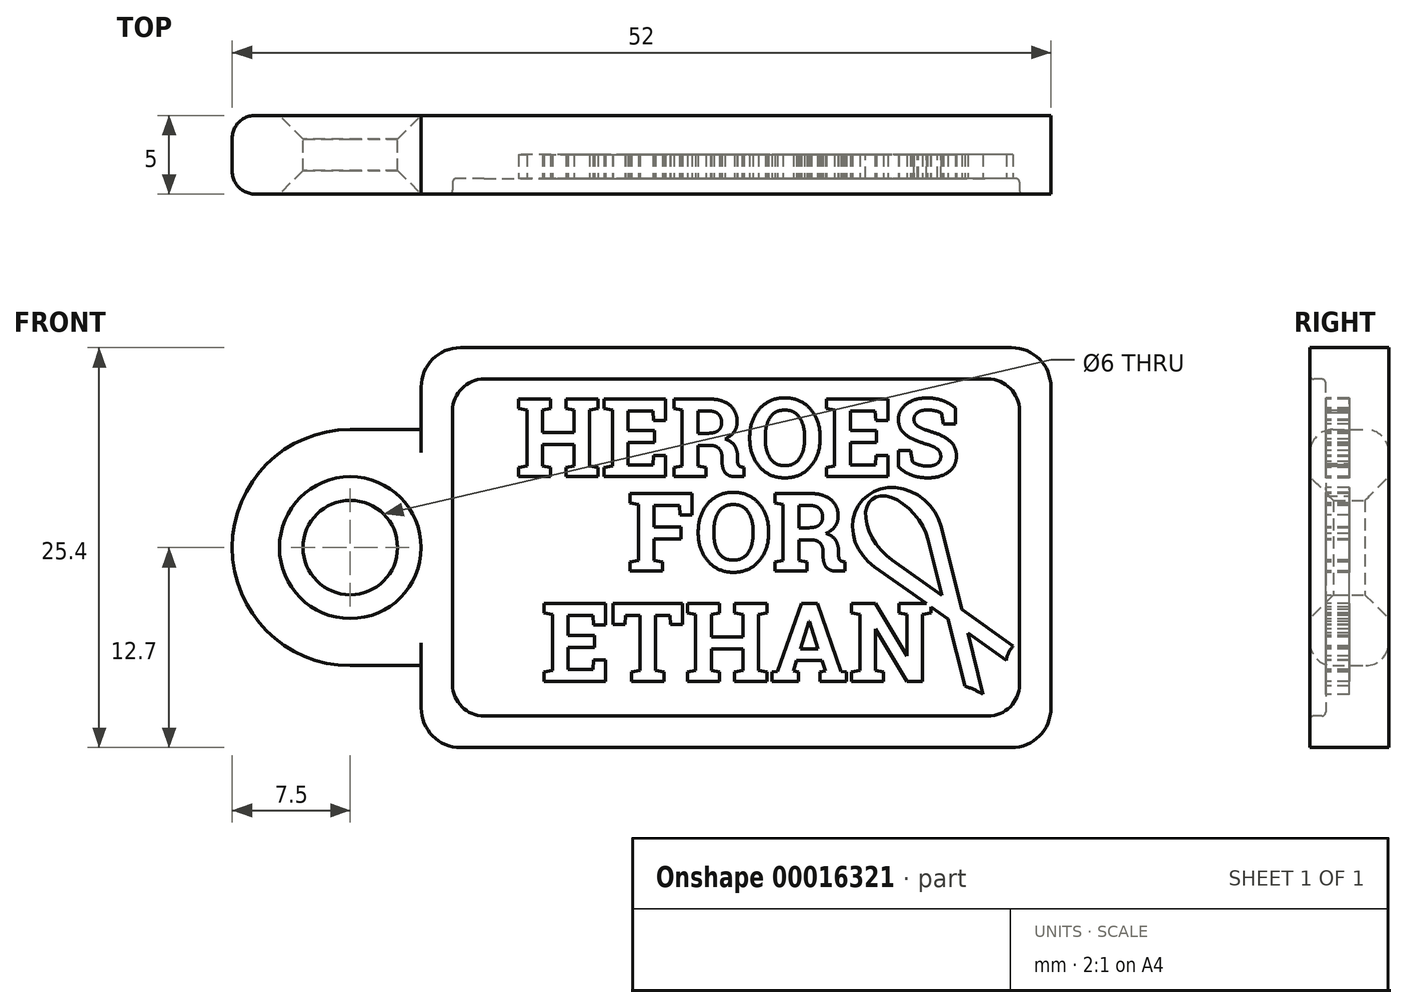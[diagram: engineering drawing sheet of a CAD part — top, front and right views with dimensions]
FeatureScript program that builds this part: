
annotation { "Feature Type Name" : "Feature", "Feature Type Description" : "" }
export const myFeature = defineFeature(function(context is Context, id is Id, definition is map)
    precondition{}
    {
        {
            var Q0;
            Q0=qCreatedBy(makeId("Top.planeOp"),FACE);
            var sketch = newSketch(context, id + "F0", { "sketchPlane" : qUnion([Q0])});
            skLineSegment(sketch, "E0", {"start": v(20, 2.5) * mm, "end": v(20, -2.5) * mm});
            skLineSegment(sketch, "E1", {"start": v(-20, 2.5) * mm, "end": v(-20, -2.5) * mm});
            skLineSegment(sketch, "E2", {"start": v(-20, -2.5) * mm, "end": v(20, -2.5) * mm});
            skLineSegment(sketch, "E3", {"start": v(-20, 2.5) * mm, "end": v(20, 2.5) * mm});
            skLineSegment(sketch, "E4", {"start": v(-20, 0) * mm, "end": v(20, 0) * mm});
            skSolve(sketch);
        }
        {
            var Q0;
            {var subQ1=sQuery(id+"F0.wireOp",EDGE,"E3");Q0=makeQuery(id+"F0.imprint","IMPRINT",FACE,{"disambiguationData":[TD([[makeQuery(id+"F0.imprint","IMPRINT",EDGE,{"derivedFrom":subQ1}),-1.0]])]});}
            var Q1;
            {var subQ1=sQuery(id+"F0.wireOp",EDGE,"E2");Q1=makeQuery(id+"F0.imprint","IMPRINT",FACE,{"disambiguationData":[TD([[makeQuery(id+"F0.imprint","IMPRINT",EDGE,{"derivedFrom":subQ1}),1.0]])]});}
            extrude(context, id + "F1", {"entities" : qUnion([Q0, Q1]), "depth" : 25.4 * mm, "symmetric" : true});
        }
        {
            var Q0;
            Q0=makeQuery(id+"F1.opExtrude","SWEPT_FACE",FACE,{"disambiguationData":[OSD([sQuery(id+"F0.wireOp",EDGE,"E2")])]});
            var sketch = newSketch(context, id + "F2", { "sketchPlane" : qUnion([Q0])});
            skLineSegment(sketch, "E5.0", {"start": v(-18, 10.7) * mm, "end": v(18, 10.7) * mm});
            skLineSegment(sketch, "E5.1", {"start": v(-18, 10.7) * mm, "end": v(-18, -10.7) * mm});
            skLineSegment(sketch, "E5.2", {"start": v(-18, -10.7) * mm, "end": v(18, -10.7) * mm});
            skLineSegment(sketch, "E5.3", {"start": v(18, 10.7) * mm, "end": v(18, -10.7) * mm});
            skSolve(sketch);
        }
        {
            var Q0;
            Q0=sQuery(id+"F0.wireOp",EDGE,"E4");
            var Q1;
            Q1=makeQuery(id+"F1.opExtrude","SWEPT_BODY",BODY,{"disambiguationData":[OSD([sQuery(id+"F0.wireOp",EDGE,"E0"),sQuery(id+"F0.wireOp",EDGE,"E1"),sQuery(id+"F0.wireOp",EDGE,"E2"),sQuery(id+"F0.wireOp",EDGE,"E3")])]});
            var Q2;
            Q2=makeQuery(id+"F1.opExtrude","SWEPT_BODY",BODY,{"disambiguationData":[OSD([sQuery(id+"F0.wireOp",EDGE,"3ae86715-4597-4b07-991b-ed0a3d32f982"),sQuery(id+"F0.wireOp",EDGE,"698c7477-3518-489a-9b49-7b4782697e80.0"),sQuery(id+"F0.wireOp",EDGE,"E0"),sQuery(id+"F0.wireOp",EDGE,"E1")])]});
            extrude(context, id + "F3", {"bodyType" : ToolBodyType.SURFACE, "surfaceEntities" : qUnion([Q0]), "endBound" : BoundingType.UP_TO_BODY, "endBoundEntityBody" : qUnion([Q1]), "depth" : 25 * mm, "hasSecondDirection" : true, "secondDirectionBound" : BoundingType.UP_TO_BODY, "secondDirectionOppositeDirection" : true, "secondDirectionBoundEntityBody" : qUnion([Q2]), "secondDirectionDepth" : 25 * mm});
        }
        {
            var Q0;
            Q0=qCreatedBy(makeId("Front.planeOp"),FACE);
            cPlane(context, id + "F4", {"entities" : qUnion([Q0]), "cplaneType" : CPlaneType.OFFSET, "offset" : 5 * mm, "width" : 150 * mm, "height" : 150 * mm});
        }
        {
            var Q0;
            Q0=qCreatedBy(id+"F4.planeOp",FACE);
            var sketch = newSketch(context, id + "F5", { "sketchPlane" : qUnion([Q0])});
            skText(sketch, "E6", { "text": "HEROES", "fontName": "RobotoSlab-Bold.ttf"});
            const initialGuessF5  = {"E6": [-0.014, 0.0045, 1, 0, 0.005]};
            skSetInitialGuess(sketch, initialGuessF5);
            skSolve(sketch);
        }
        {
            var Q0;
            Q0=qCreatedBy(id+"F4.planeOp",FACE);
            var sketch = newSketch(context, id + "F6", { "sketchPlane" : qUnion([Q0])});
            skText(sketch, "E7", { "text": "FOR", "fontName": "RobotoSlab-Bold.ttf"});
            const initialGuessF6  = {"E7": [-0.00692, -0.0015, 1, 0, 0.005]};
            skSetInitialGuess(sketch, initialGuessF6);
            skSolve(sketch);
        }
        {
            var Q0;
            Q0=qCreatedBy(id+"F4.planeOp",FACE);
            var sketch = newSketch(context, id + "F7", { "sketchPlane" : qUnion([Q0])});
            skText(sketch, "E8", { "text": "ETHAN", "fontName": "RobotoSlab-Bold.ttf"});
            const initialGuessF7  = {"E8": [-0.01238, -0.0085, 1, 0, 0.005]};
            skSetInitialGuess(sketch, initialGuessF7);
            skSolve(sketch);
        }
        {
            var Q0;
            Q0=makeQuery(id+"F5.imprint","IMPRINT",FACE,{"disambiguationData":[TD([[makeQuery(id+"F5.imprint","IMPRINT",EDGE,{"derivedFrom":sQuery(id+"F5.wireOp",EDGE,"E6.sketch_text.stroke-0")}),-1.0]])]});
            var Q1;
            Q1=makeQuery(id+"F5.imprint","IMPRINT",FACE,{"disambiguationData":[TD([[makeQuery(id+"F5.imprint","IMPRINT",EDGE,{"derivedFrom":sQuery(id+"F5.wireOp",EDGE,"E6.sketch_text.stroke-30")}),-1.0]])]});
            var Q2;
            Q2=makeQuery(id+"F5.imprint","IMPRINT",FACE,{"disambiguationData":[TD([[makeQuery(id+"F5.imprint","IMPRINT",EDGE,{"derivedFrom":sQuery(id+"F5.wireOp",EDGE,"E6.sketch_text.stroke-51")}),-1.0]])]});
            var Q3;
            Q3=makeQuery(id+"F5.imprint","IMPRINT",FACE,{"disambiguationData":[TD([[makeQuery(id+"F5.imprint","IMPRINT",EDGE,{"derivedFrom":sQuery(id+"F5.wireOp",EDGE,"E6.sketch_text.stroke-107")}),-1.0]])]});
            var Q4;
            Q4=makeQuery(id+"F5.imprint","IMPRINT",FACE,{"disambiguationData":[TD([[makeQuery(id+"F5.imprint","IMPRINT",EDGE,{"derivedFrom":sQuery(id+"F5.wireOp",EDGE,"E6.sketch_text.stroke-128")}),-1.0]])]});
            var Q5;
            Q5=makeQuery(id+"F5.imprint","IMPRINT",FACE,{"disambiguationData":[TD([[makeQuery(id+"F5.imprint","IMPRINT",EDGE,{"derivedFrom":sQuery(id+"F5.wireOp",EDGE,"E6.sketch_text.stroke-87")}),-1.0]])]});
            var Q6;
            Q6=makeQuery(id+"F6.imprint","IMPRINT",FACE,{"disambiguationData":[TD([[makeQuery(id+"F6.imprint","IMPRINT",EDGE,{"derivedFrom":sQuery(id+"F6.wireOp",EDGE,"E7.sketch_text.stroke-0")}),-1.0]])]});
            var Q7;
            Q7=makeQuery(id+"F6.imprint","IMPRINT",FACE,{"disambiguationData":[TD([[makeQuery(id+"F6.imprint","IMPRINT",EDGE,{"derivedFrom":sQuery(id+"F6.wireOp",EDGE,"E7.sketch_text.stroke-18")}),-1.0]])]});
            var Q8;
            Q8=makeQuery(id+"F6.imprint","IMPRINT",FACE,{"disambiguationData":[TD([[makeQuery(id+"F6.imprint","IMPRINT",EDGE,{"derivedFrom":sQuery(id+"F6.wireOp",EDGE,"E7.sketch_text.stroke-38")}),-1.0]])]});
            var Q9;
            Q9=makeQuery(id+"F7.imprint","IMPRINT",FACE,{"disambiguationData":[TD([[makeQuery(id+"F7.imprint","IMPRINT",EDGE,{"derivedFrom":sQuery(id+"F7.wireOp",EDGE,"E8.sketch_text.stroke-0")}),-1.0]])]});
            var Q10;
            Q10=makeQuery(id+"F7.imprint","IMPRINT",FACE,{"disambiguationData":[TD([[makeQuery(id+"F7.imprint","IMPRINT",EDGE,{"derivedFrom":sQuery(id+"F7.wireOp",EDGE,"E8.sketch_text.stroke-21")}),-1.0]])]});
            var Q11;
            Q11=makeQuery(id+"F7.imprint","IMPRINT",FACE,{"disambiguationData":[TD([[makeQuery(id+"F7.imprint","IMPRINT",EDGE,{"derivedFrom":sQuery(id+"F7.wireOp",EDGE,"E8.sketch_text.stroke-37")}),-1.0]])]});
            var Q12;
            Q12=makeQuery(id+"F7.imprint","IMPRINT",FACE,{"disambiguationData":[TD([[makeQuery(id+"F7.imprint","IMPRINT",EDGE,{"derivedFrom":sQuery(id+"F7.wireOp",EDGE,"E8.sketch_text.stroke-67")}),-1.0]])]});
            var Q13;
            Q13=makeQuery(id+"F7.imprint","IMPRINT",FACE,{"disambiguationData":[TD([[makeQuery(id+"F7.imprint","IMPRINT",EDGE,{"derivedFrom":sQuery(id+"F7.wireOp",EDGE,"E8.sketch_text.stroke-87")}),-1.0]])]});
            var Q14;
            Q14=makeQuery(id+"F3.opExtrude","SWEPT_FACE",FACE,{"disambiguationData":[OSD([sQuery(id+"F0.wireOp",EDGE,"E4")])]});
            extrude(context, id + "F8", {"entities" : qUnion([Q0, Q1, Q2, Q3, Q4, Q5, Q6, Q7, Q8, Q9, Q10, Q11, Q12, Q13]), "operationType" : NewBodyOperationType.REMOVE, "endBound" : BoundingType.UP_TO_SURFACE, "oppositeDirection" : true, "endBoundEntityFace" : qUnion([Q14]), "depth" : 25 * mm});
        }
        {
            var Q0;
            Q0=qCreatedBy(makeId("Front.planeOp"),FACE);
            var sketch = newSketch(context, id + "F9", { "sketchPlane" : qUnion([Q0])});
            skCircle(sketch, "E9", {"center": v(-24.5, 0) * mm, "radius": 3 * mm});
            skArc(sketch, "E10", {"start": v(-24.5, 7.5) * mm, "mid": v(-32, 0) * mm, "end": v(-24.5, -7.5) * mm});
            skLineSegment(sketch, "E11", {"start": v(-24.5, 7.5) * mm, "end": v(-20, 7.5) * mm});
            skLineSegment(sketch, "E12", {"start": v(-24.5, -7.5) * mm, "end": v(-20, -7.5) * mm});
            skLineSegment(sketch, "E13", {"start": v(-20, 7.5) * mm, "end": v(-20, -7.5) * mm});
            skLineSegment(sketch, "E14.MirrorCS", {"start": v(20, 7.5) * mm, "end": v(20, -7.5) * mm});
            skLineSegment(sketch, "E15.MirrorCS", {"start": v(24.5, 7.5) * mm, "end": v(20, 7.5) * mm});
            skLineSegment(sketch, "E16.MirrorCS", {"start": v(24.5, -7.5) * mm, "end": v(20, -7.5) * mm});
            skCircle(sketch, "E17.MirrorC", {"center": v(24.5, 0) * mm, "radius": 3 * mm});
            skArc(sketch, "E18.MirrorCS", {"start": v(24.5, 7.5) * mm, "mid": v(32, 0) * mm, "end": v(24.5, -7.5) * mm});
            skSolve(sketch);
        }
        {
            var Q0;
            Q0=makeQuery(id+"F9.imprint","IMPRINT",FACE,{"disambiguationData":[TD([[makeQuery(id+"F9.imprint","IMPRINT",EDGE,{"derivedFrom":sQuery(id+"F9.wireOp",EDGE,"E9")}),-1.0]])]});
            var Q1;
            {var subQ2=sQuery(id+"F0.wireOp",EDGE,"E2");var subQ3=sQuery(id+"F0.wireOp",EDGE,"E0");Q1=makeQuery(id+"F8.boolean.opBoolean","SPLIT",FACE,{"disambiguationData":[TD([makeQuery(id+"F1.opExtrude","SWEPT_FACE",FACE,{"disambiguationData":[OSD([subQ3])]})])],"derivedFrom":makeQuery(id+"F1.opExtrude","SWEPT_FACE",FACE,{"disambiguationData":[OSD([subQ2])]})});}
            var Q2;
            Q2=makeQuery(id+"F1.opExtrude","SWEPT_FACE",FACE,{"disambiguationData":[OSD([sQuery(id+"F0.wireOp",EDGE,"E3")])]});
            extrude(context, id + "F10", {"entities" : qUnion([Q0]), "operationType" : NewBodyOperationType.ADD, "endBound" : BoundingType.UP_TO_SURFACE, "endBoundEntityFace" : qUnion([Q1]), "depth" : 25 * mm, "hasSecondDirection" : true, "secondDirectionBound" : BoundingType.UP_TO_SURFACE, "secondDirectionOppositeDirection" : true, "secondDirectionBoundEntityFace" : qUnion([Q2]), "secondDirectionDepth" : 25 * mm});
        }
        {
            var Q0;
            Q0=makeQuery(id+"F1.opExtrude","CAP_EDGE",EDGE,{"disambiguationData":[OSD([sQuery(id+"F0.wireOp",EDGE,"E0")])],"isStart":false});
            var Q1;
            Q1=makeQuery(id+"F1.opExtrude","CAP_EDGE",EDGE,{"disambiguationData":[OSD([sQuery(id+"F0.wireOp",EDGE,"E0")])],"isStart":true});
            var Q2;
            Q2=makeQuery(id+"F1.opExtrude","CAP_EDGE",EDGE,{"disambiguationData":[OSD([sQuery(id+"F0.wireOp",EDGE,"E1")])],"isStart":false});
            var Q3;
            Q3=makeQuery(id+"F10.opExtrude","TWEAK_EDGE",EDGE,{"derivedFrom":[makeQuery(id+"F9.imprint","IMPRINT",EDGE,{"derivedFrom":sQuery(id+"F9.wireOp",EDGE,"E11")}),makeQuery(id+"F9.imprint","IMPRINT",EDGE,{"derivedFrom":sQuery(id+"F9.wireOp",EDGE,"E13")})]});
            var Q4;
            Q4=makeQuery(id+"F10.opExtrude","TWEAK_EDGE",EDGE,{"derivedFrom":[makeQuery(id+"F9.imprint","IMPRINT",EDGE,{"derivedFrom":sQuery(id+"F9.wireOp",EDGE,"E12")}),makeQuery(id+"F9.imprint","IMPRINT",EDGE,{"derivedFrom":sQuery(id+"F9.wireOp",EDGE,"E13")})]});
            var Q5;
            Q5=makeQuery(id+"F1.opExtrude","CAP_EDGE",EDGE,{"disambiguationData":[OSD([sQuery(id+"F0.wireOp",EDGE,"E1")])],"isStart":true});
            fillet(context, id + "F11", {"entities" : qUnion([Q0, Q1, Q2, Q3, Q4, Q5]), "radius" : 2.5 * mm, "tangentPropagation" : true, "allowEdgeOverflow" : false});
        }
        {
            var Q0;
            Q0=makeQuery(id+"F10.opExtrude","CAP_EDGE",EDGE,{"disambiguationData":[OSD([sQuery(id+"F9.wireOp",EDGE,"E9")])],"isStart":false});
            var Q1;
            Q1=makeQuery(id+"F10.opExtrude","CAP_EDGE",EDGE,{"disambiguationData":[OSD([sQuery(id+"F9.wireOp",EDGE,"E9")])],"isStart":true});
            chamfer(context, id + "F12", {"entities" : qUnion([Q0, Q1]), "width" : 1.5 * mm, "tangentPropagation" : true});
        }
        {
            var Q0;
            Q0=qCreatedBy(id+"F4.planeOp",FACE);
            var sketch = newSketch(context, id + "F13", { "sketchPlane" : qUnion([Q0])});
            skEllipticalArc(sketch, "E19", {});
            skEllipticalArc(sketch, "E20", {});
            skLineSegment(sketch, "E21", {"start": v(13.01, 1.36) * mm, "end": v(14.34, -3.94) * mm});
            skLineSegment(sketch, "E22", {"start": v(8.78, -1.22) * mm, "end": v(13.46, -4.54) * mm});
            skLineSegment(sketch, "E23", {"start": v(12.2, 0.51) * mm, "end": v(13.09, -3.05) * mm});
            skLineSegment(sketch, "E24", {"start": v(9.9, -0.79) * mm, "end": v(13.09, -3.05) * mm});
            skLineSegment(sketch, "E25.trimOffspring", {"start": v(14.34, -3.94) * mm, "end": v(17.6, -6.26) * mm});
            skLineSegment(sketch, "E26.trimOffspring", {"start": v(14.71, -5.43) * mm, "end": v(17.16, -7.17) * mm});
            skLineSegment(sketch, "E27.trimOffspring", {"start": v(14.71, -5.43) * mm, "end": v(15.69, -9.32) * mm});
            skLineSegment(sketch, "E28.trimOffspring", {"start": v(13.46, -4.54) * mm, "end": v(14.52, -8.8) * mm});
            skArc(sketch, "E29", {"start": v(17.6, -6.26) * mm, "mid": v(17.31, -6.68) * mm, "end": v(17.16, -7.17) * mm});
            skLineSegment(sketch, "E30", {"start": v(10.25, 1) * mm, "end": v(13.09, -3.05) * mm, "construction": true});
            skLineSegment(sketch, "E31", {"start": v(14.71, -5.43) * mm, "end": v(13.09, -3.05) * mm, "construction": true});
            skArc(sketch, "E32", {"start": v(15.69, -9.32) * mm, "mid": v(15.12, -9.02) * mm, "end": v(14.52, -8.8) * mm});
            const initialGuessF13  = {"E19": [0.01025, 0.001, 0.7887906643900963, 0.6146619296581094, 0.0015443011344752802, 0.0026264673633837167, 5.637913367309432, 3.6133603210792997], "E20": [0.01025, 0.001, 0.669353291916386, 0.7429442580710193, 0.0026556683538861807, 0.003, 5.6333376813169505, 3.2724019014194843]};
            skSetInitialGuess(sketch, initialGuessF13);
            skSolve(sketch);
        }
        {
            var Q0;
            Q0=makeQuery(id+"F13.imprint","IMPRINT",FACE,{"disambiguationData":[TD([[makeQuery(id+"F13.imprint","IMPRINT",EDGE,{"derivedFrom":sQuery(id+"F13.wireOp",EDGE,"E19")}),-1.0]])]});
            var Q1;
            Q1=makeQuery(id+"F3.opExtrude","SWEPT_FACE",FACE,{"disambiguationData":[OSD([sQuery(id+"F0.wireOp",EDGE,"E4")])]});
            extrude(context, id + "F14", {"entities" : qUnion([Q0]), "operationType" : NewBodyOperationType.REMOVE, "endBound" : BoundingType.UP_TO_SURFACE, "oppositeDirection" : true, "endBoundEntityFace" : qUnion([Q1]), "depth" : 25 * mm});
        }
        {
            var Q0;
            Q0=makeQuery(id+"F2.imprint","IMPRINT",FACE,{"disambiguationData":[TD([[makeQuery(id+"F2.imprint","IMPRINT",EDGE,{"derivedFrom":sQuery(id+"F2.wireOp",EDGE,"E5.0")}),-1.0]])]});
            var Q1;
            Q1 = qConstructionFilter(qBodyType(qCreatedBy(id + "F2" ,EDGE), BodyType.WIRE), ConstructionObject.NO);
            extrude(context, id + "F15", {"entities" : qUnion([Q0]), "operationType" : NewBodyOperationType.REMOVE, "surfaceEntities" : qUnion([Q1]), "oppositeDirection" : true, "depth" : 1 * mm});
        }
        {
            var Q0;
            Q0=makeQuery(id+"F10.opExtrude","CAP_EDGE",EDGE,{"disambiguationData":[OSD([sQuery(id+"F9.wireOp",EDGE,"E10")])],"isStart":false});
            var Q1;
            Q1=makeQuery(id+"F10.opExtrude","CAP_EDGE",EDGE,{"disambiguationData":[OSD([sQuery(id+"F9.wireOp",EDGE,"E10")])],"isStart":true});
            fillet(context, id + "F16", {"entities" : qUnion([Q0, Q1]), "radius" : 1.45 * mm, "tangentPropagation" : true, "allowEdgeOverflow" : false});
        }
        {
            var Q0;
            Q0=makeQuery(id+"F15.boolean.opBoolean","COPY",EDGE,{"derivedFrom":makeQuery(id+"F15.opExtrude","SWEPT_EDGE",EDGE,{"disambiguationData":[OSD([sQuery(id+"F2.wireOp",EDGE,"E5.0"),sQuery(id+"F2.wireOp",EDGE,"E5.1")])]})});
            var Q1;
            Q1=makeQuery(id+"F15.boolean.opBoolean","COPY",EDGE,{"derivedFrom":makeQuery(id+"F15.opExtrude","SWEPT_EDGE",EDGE,{"disambiguationData":[OSD([sQuery(id+"F2.wireOp",EDGE,"E5.0"),sQuery(id+"F2.wireOp",EDGE,"E5.3")])]})});
            var Q2;
            Q2=makeQuery(id+"F15.boolean.opBoolean","COPY",EDGE,{"derivedFrom":makeQuery(id+"F15.opExtrude","SWEPT_EDGE",EDGE,{"disambiguationData":[OSD([sQuery(id+"F2.wireOp",EDGE,"E5.2"),sQuery(id+"F2.wireOp",EDGE,"E5.3")])]})});
            var Q3;
            Q3=makeQuery(id+"F15.boolean.opBoolean","COPY",EDGE,{"derivedFrom":makeQuery(id+"F15.opExtrude","SWEPT_EDGE",EDGE,{"disambiguationData":[OSD([sQuery(id+"F2.wireOp",EDGE,"E5.1"),sQuery(id+"F2.wireOp",EDGE,"E5.2")])]})});
            fillet(context, id + "F17", {"entities" : qUnion([Q0, Q1, Q2, Q3]), "radius" : 2 * mm, "tangentPropagation" : true, "allowEdgeOverflow" : false});
        }
        {
            var Q0;
            {var subQ94=sQuery(id+"F9.wireOp",EDGE,"E13");var subQ95=sQuery(id+"F9.wireOp",EDGE,"E12");var subQ98=sQuery(id+"F9.wireOp",EDGE,"E11");var subQ106=sQuery(id+"F0.wireOp",EDGE,"E0");var subQ143=makeQuery(id+"F1.opExtrude","SWEPT_FACE",FACE,{"disambiguationData":[OSD([subQ106])]});var subQ148=sQuery(id+"F0.wireOp",EDGE,"E2");var subQ169=sQuery(id+"F9.wireOp",EDGE,"E10");var subQ306=sQuery(id+"F9.wireOp",EDGE,"E9");Q0=makeQuery(id+"F17.opFillet","BLEND_EDGE",EDGE,{"blendedFrom":[makeQuery(id+"F15.boolean.opBoolean","COPY",EDGE,{"derivedFrom":makeQuery(id+"F15.opExtrude","SWEPT_EDGE",EDGE,{"disambiguationData":[OSD([sQuery(id+"F2.wireOp",EDGE,"E5.0"),sQuery(id+"F2.wireOp",EDGE,"E5.1")])]})}),makeQuery(id+"F14.boolean.opBoolean","SPLIT",FACE,{"disambiguationData":[TD([subQ143])],"derivedFrom":makeQuery(id+"F10.boolean.opBoolean","MERGE",FACE,{"derivedFrom":[makeQuery(id+"F8.boolean.opBoolean","SPLIT",FACE,{"disambiguationData":[TD([subQ143])],"derivedFrom":makeQuery(id+"F1.opExtrude","SWEPT_FACE",FACE,{"disambiguationData":[OSD([subQ148])]})}),makeQuery(id+"F10.opExtrude","CAP_FACE",FACE,{"disambiguationData":[OSD([subQ306,subQ169,subQ98,subQ95,subQ94])],"isStart":false})]})})],"blendedInto":[makeQuery(id+"F14.boolean.opBoolean","SPLIT",FACE,{"disambiguationData":[TD([subQ143])],"derivedFrom":makeQuery(id+"F10.boolean.opBoolean","MERGE",FACE,{"derivedFrom":[makeQuery(id+"F8.boolean.opBoolean","SPLIT",FACE,{"disambiguationData":[TD([subQ143])],"derivedFrom":makeQuery(id+"F1.opExtrude","SWEPT_FACE",FACE,{"disambiguationData":[OSD([subQ148])]})}),makeQuery(id+"F10.opExtrude","CAP_FACE",FACE,{"disambiguationData":[OSD([subQ306,subQ169,subQ98,subQ95,subQ94])],"isStart":false})]})})]});}
            var Q1;
            {var subQ0=sQuery(id+"F2.wireOp",EDGE,"E5.0");var subQ1=sQuery(id+"F2.wireOp",EDGE,"E5.1");Q1=makeQuery(id+"F17.opFillet","BLEND_EDGE",EDGE,{"blendedFrom":[makeQuery(id+"F15.boolean.opBoolean","COPY",EDGE,{"derivedFrom":makeQuery(id+"F15.opExtrude","SWEPT_EDGE",EDGE,{"disambiguationData":[OSD([subQ0,subQ1])]})}),makeQuery(id+"F15.boolean.opBoolean","COPY",FACE,{"disambiguationData":[OD(6.0)],"derivedFrom":makeQuery(id+"F15.opExtrude","CAP_FACE",FACE,{"disambiguationData":[OSD([subQ0,subQ1,sQuery(id+"F2.wireOp",EDGE,"E5.2"),sQuery(id+"F2.wireOp",EDGE,"E5.3")])],"isStart":false})})],"blendedInto":[makeQuery(id+"F15.boolean.opBoolean","COPY",FACE,{"disambiguationData":[OD(6.0)],"derivedFrom":makeQuery(id+"F15.opExtrude","CAP_FACE",FACE,{"disambiguationData":[OSD([subQ0,subQ1,sQuery(id+"F2.wireOp",EDGE,"E5.2"),sQuery(id+"F2.wireOp",EDGE,"E5.3")])],"isStart":false})})]});}
            fillet(context, id + "F18", {"entities" : qUnion([Q0, Q1]), "radius" : .25 * mm, "tangentPropagation" : true, "allowEdgeOverflow" : false});
        }
    });
